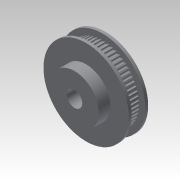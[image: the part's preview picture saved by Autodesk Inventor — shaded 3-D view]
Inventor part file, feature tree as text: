
AUTODESK INVENTOR PART (.ipt)
format: ipt  version: 2020 (Build 240168000, 168)  size: 247,808 bytes
history: native  units: mm
features: sketch x2, revolve x1, extrude x1, pattern_circular x1
ambient origin geometry x8: Origin, YZ Plane, XZ Plane, XY Plane, X Axis, Y Axis, Z Axis, Center Point
bodies: Solid1 (feature_tree)
feature tree (5):
  revolve  "Revolution1"  [1 undecoded]
  extrude  "Extrusion1"  Depth=18.95mm
  pattern_circular  "Circular Pattern1"  Angle=90.0deg  [1 undecoded]
  sketch  "Sketch1"  dims[d0=4.0mm d1=7.0mm]
  sketch  "Sketch2"  dims[d4=1.5mm d6=18.95mm d7=90.0deg d8=1.3mm d9=18.85mm d10=10.0mm d11=0.0mm d12=600.0mm d13=360.0deg d15=22.0mm d16=6.0mm d17=12.5mm]
note: 2 required parameter values undecoded (feature->parameter linkage not recoverable at this tier; creation-order binding heuristic only, values carry confidence <= 0.55)